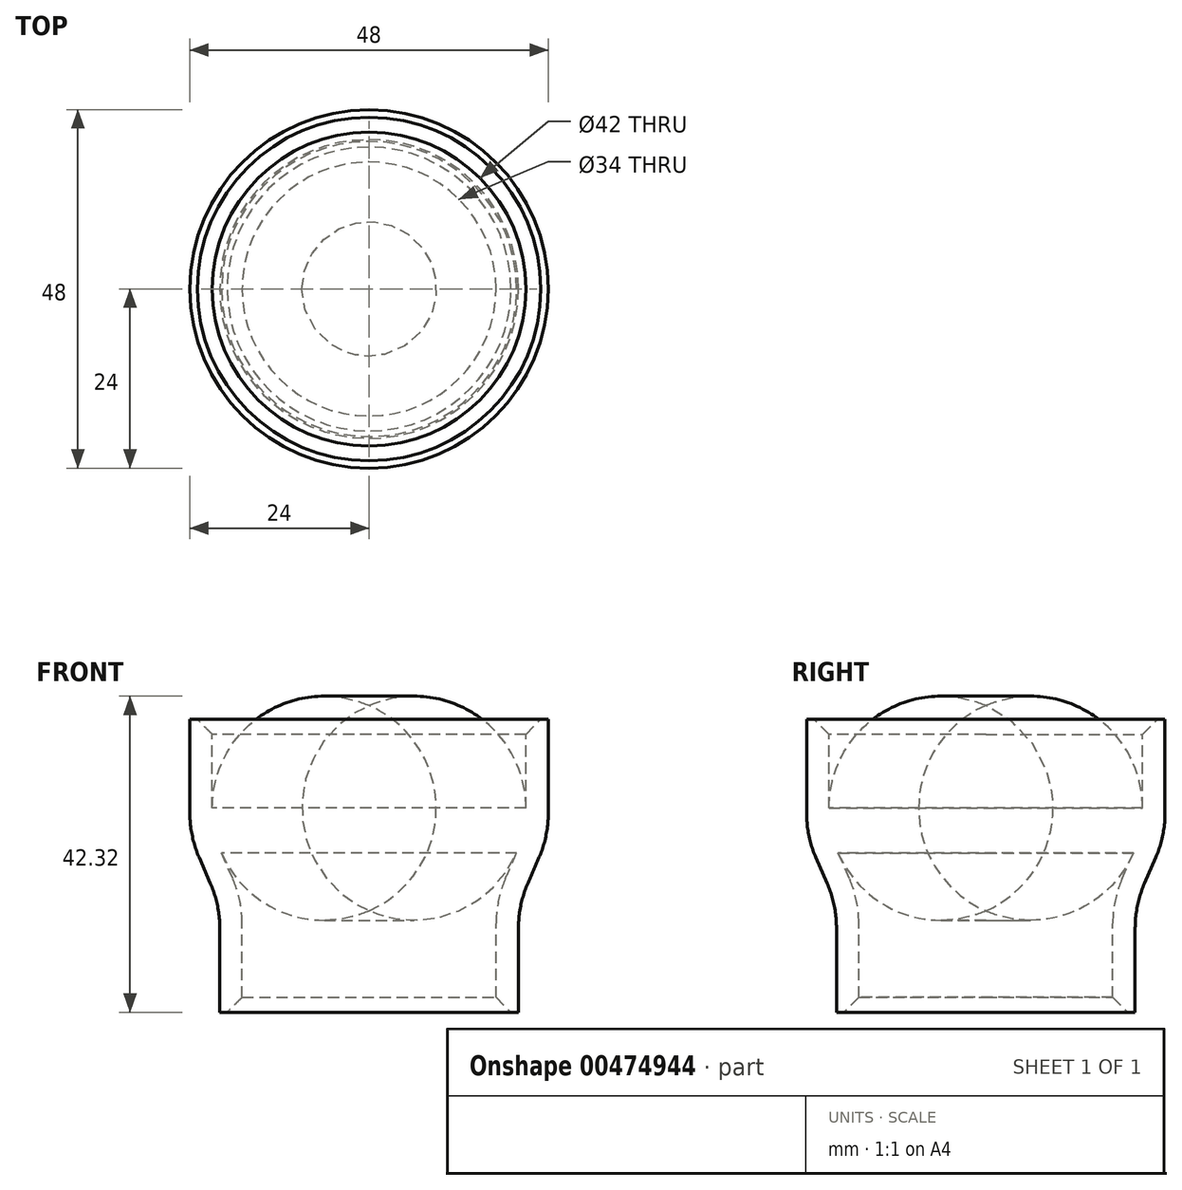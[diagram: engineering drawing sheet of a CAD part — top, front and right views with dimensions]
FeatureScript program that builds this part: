
annotation { "Feature Type Name" : "Feature", "Feature Type Description" : "" }
export const myFeature = defineFeature(function(context is Context, id is Id, definition is map)
    precondition{}
    {
        {
            var Q0;
            Q0=qCreatedBy(makeId("Front.planeOp"),FACE);
            var sketch = newSketch(context, id + "F0", { "sketchPlane" : qUnion([Q0])});
            skLineSegment(sketch, "E0", {"start": v(21, 24.2) * mm, "end": v(21, 9.2) * mm});
            skLineSegment(sketch, "E1", {"start": v(21, 9.2) * mm, "end": v(17, 0) * mm});
            skLineSegment(sketch, "E2", {"start": v(17, 0) * mm, "end": v(17, -15) * mm});
            skLineSegment(sketch, "E3.0", {"start": v(20, -0.62) * mm, "end": v(20, -15) * mm});
            skLineSegment(sketch, "E3.1", {"start": v(24, 8.57) * mm, "end": v(20, -0.62) * mm});
            skLineSegment(sketch, "E3.2", {"start": v(24, 24.2) * mm, "end": v(24, 8.57) * mm});
            skLineSegment(sketch, "E4", {"start": v(24, 24.2) * mm, "end": v(21, 24.2) * mm});
            skLineSegment(sketch, "E5", {"start": v(20, -15) * mm, "end": v(17, -15) * mm});
            skLineSegment(sketch, "E6", {"start": v(0, 33.25) * mm, "end": v(0, -23) * mm, "construction": true});
            skSolve(sketch);
        }
        {
            var Q0;
            Q0 = qSketchRegion(id + "F0", true);
            var Q1;
            Q1=sQuery(id+"F0.wireOp",EDGE,"E6");
            revolve(context, id + "F1", {"entities" : qUnion([Q0]), "axis" : qUnion([Q1]), "revolveType" : RevolveType.FULL});
        }
        {
            var Q0;
            Q0=makeQuery(id+"F1.opRevolve","SWEPT_EDGE",EDGE,{"disambiguationData":[OSD([sQuery(id+"F0.wireOp",EDGE,"E3.0"),sQuery(id+"F0.wireOp",EDGE,"E3.1")])]});
            var Q1;
            Q1=makeQuery(id+"F1.opRevolve","SWEPT_EDGE",EDGE,{"disambiguationData":[OSD([sQuery(id+"F0.wireOp",EDGE,"E3.1"),sQuery(id+"F0.wireOp",EDGE,"E3.2")])]});
            var Q2;
            Q2=makeQuery(id+"F1.opRevolve","SWEPT_EDGE",EDGE,{"disambiguationData":[OSD([sQuery(id+"F0.wireOp",EDGE,"E0"),sQuery(id+"F0.wireOp",EDGE,"E1")])]});
            var Q3;
            Q3=makeQuery(id+"F1.opRevolve","SWEPT_EDGE",EDGE,{"disambiguationData":[OSD([sQuery(id+"F0.wireOp",EDGE,"E1"),sQuery(id+"F0.wireOp",EDGE,"E2")])]});
            fillet(context, id + "F2", {"entities" : qUnion([Q0, Q1, Q2, Q3]), "radius" : 15 * mm, "tangentPropagation" : true, "allowEdgeOverflow" : false});
        }
        {
            var Q0;
            Q0=makeQuery(id+"F1.opRevolve","SWEPT_EDGE",EDGE,{"disambiguationData":[OSD([sQuery(id+"F0.wireOp",EDGE,"E0"),sQuery(id+"F0.wireOp",EDGE,"E4")])]});
            var Q1;
            Q1=makeQuery(id+"F1.opRevolve","SWEPT_EDGE",EDGE,{"disambiguationData":[OSD([sQuery(id+"F0.wireOp",EDGE,"E2"),sQuery(id+"F0.wireOp",EDGE,"E5")])]});
            chamfer(context, id + "F3", {"entities" : qUnion([Q0, Q1]), "width" : 2 * mm, "tangentPropagation" : true});
        }
    });
